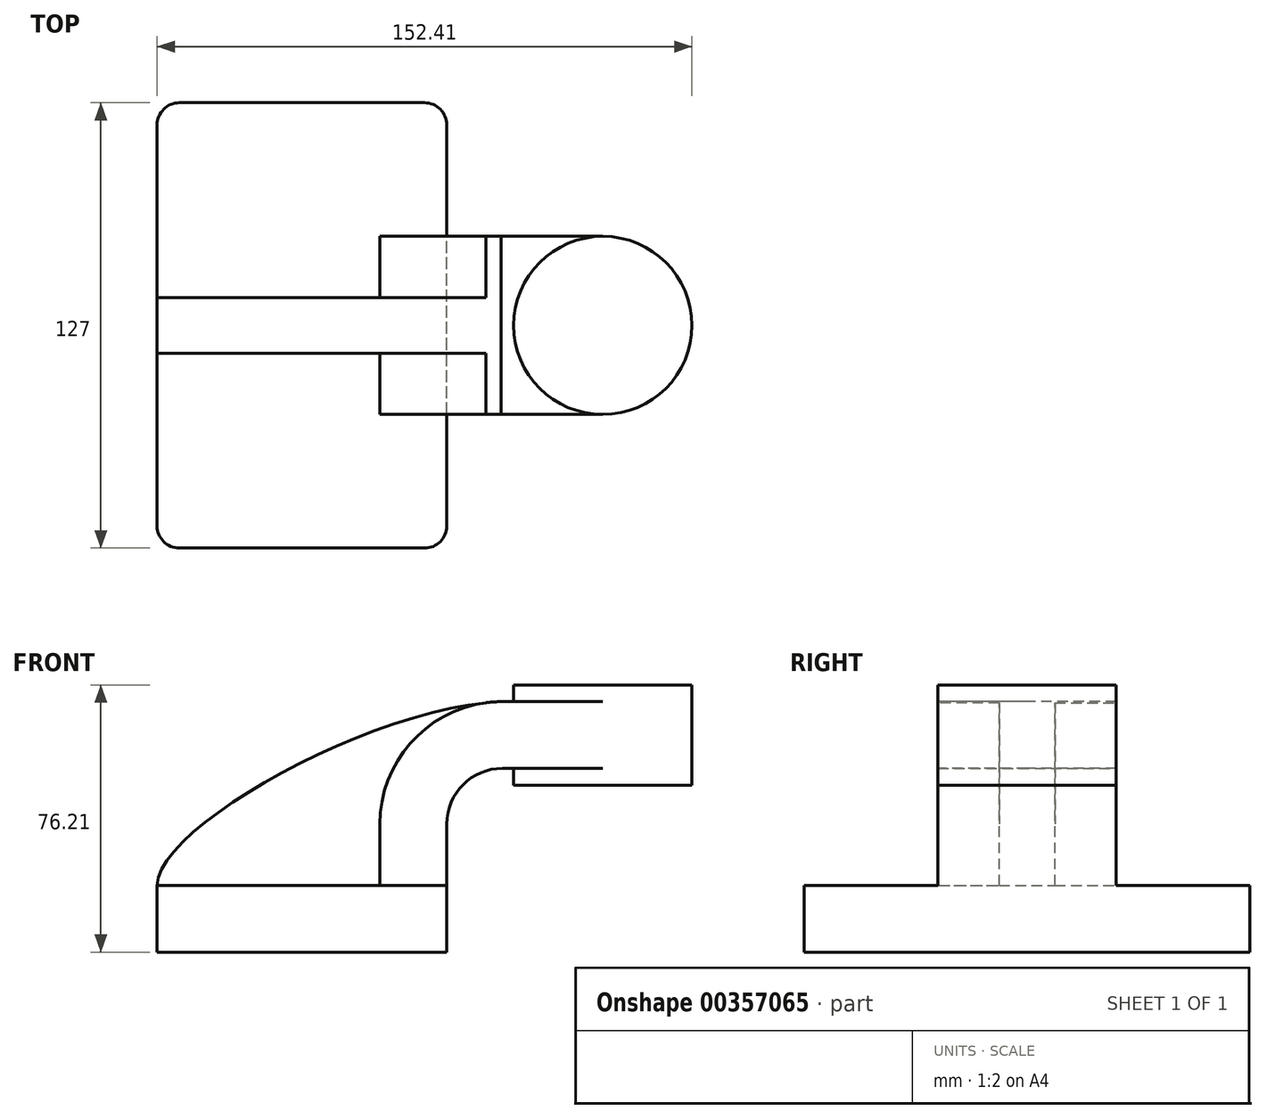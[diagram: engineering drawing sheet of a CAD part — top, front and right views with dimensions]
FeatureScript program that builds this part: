
annotation { "Feature Type Name" : "Feature", "Feature Type Description" : "" }
export const myFeature = defineFeature(function(context is Context, id is Id, definition is map)
    precondition{}
    {
        {
            var Q0;
            Q0=qCreatedBy(makeId("Front.planeOp"),FACE);
            var sketch = newSketch(context, id + "F0", { "sketchPlane" : qUnion([Q0])});
            skLineSegment(sketch, "E0.bottom", {"start": v(-41.28, 9.52) * mm, "end": v(41.27, 9.53) * mm});
            skLineSegment(sketch, "E0.top", {"start": v(-41.28, -9.53) * mm, "end": v(41.28, -9.53) * mm});
            skLineSegment(sketch, "E0.left", {"start": v(-41.28, 9.52) * mm, "end": v(-41.27, -9.53) * mm});
            skLineSegment(sketch, "E0.right", {"start": v(41.28, 9.53) * mm, "end": v(41.28, -9.52) * mm});
            skPoint(sketch, "E0.middle", {"position": v(0, 0) * mm});
            skLineSegment(sketch, "E1.bottom", {"start": v(111.12, 66.68) * mm, "end": v(60.32, 66.68) * mm});
            skLineSegment(sketch, "E1.top", {"start": v(111.12, 38.1) * mm, "end": v(60.33, 38.1) * mm});
            skLineSegment(sketch, "E1.left", {"start": v(111.12, 66.68) * mm, "end": v(111.12, 38.1) * mm});
            skLineSegment(sketch, "E1.right", {"start": v(60.32, 66.68) * mm, "end": v(60.33, 38.1) * mm});
            skPoint(sketch, "E1.middle", {"position": v(85.72, 52.39) * mm});
            skLineSegment(sketch, "E2", {"start": v(41.27, 9.53) * mm, "end": v(41.27, 27) * mm});
            skArc(sketch, "E3", {"start": v(41.27, 27) * mm, "mid": v(45.92, 38.23) * mm, "end": v(57.15, 42.88) * mm});
            skLineSegment(sketch, "E4", {"start": v(57.15, 42.88) * mm, "end": v(85.72, 42.88) * mm});
            skArc(sketch, "E5.0", {"start": v(22.22, 27) * mm, "mid": v(32.32, 51.56) * mm, "end": v(56.77, 61.92) * mm});
            skLineSegment(sketch, "E5.1", {"start": v(22.22, 9.53) * mm, "end": v(22.22, 27) * mm});
            skLineSegment(sketch, "E6", {"start": v(56.77, 61.92) * mm, "end": v(85.72, 61.92) * mm});
            skLineSegment(sketch, "E7", {"start": v(85.72, 38.1) * mm, "end": v(85.72, 66.68) * mm});
            skLineSegment(sketch, "E8", {"start": v(85.72, 66.68) * mm, "end": v(85.72, 61.92) * mm});
            skFitSpline(sketch, "E9", {"points": [v(-41.28, 9.52) * mm, v(56.77, 61.92) * mm], "startDerivative": vector(0.83, 50.51) * mm, "endDerivative": vector(110.6, 4.67) * mm});
            skSolve(sketch);
        }
        {
            var Q0;
            Q0=makeQuery(id+"F0.imprint","IMPRINT",FACE,{"disambiguationData":[TD([[makeQuery(id+"F0.imprint","IMPRINT",EDGE,{"derivedFrom":sQuery(id+"F0.wireOp",EDGE,"E0.top")}),1.0]])]});
            extrude(context, id + "F1", {"entities" : qUnion([Q0]), "endBound" : BoundingType.SYMMETRIC, "depth" : 127 * mm});
        }
        {
            var Q0;
            {var subQ1=sQuery(id+"F0.wireOp",EDGE,"E2");Q0=makeQuery(id+"F0.imprint","IMPRINT",FACE,{"disambiguationData":[TD([[makeQuery(id+"F0.imprint","IMPRINT",EDGE,{"derivedFrom":subQ1}),1.0]])]});}
            var Q1;
            {var subQ1=sQuery(id+"F0.wireOp",EDGE,"E6");var subQ3=sQuery(id+"F0.wireOp",EDGE,"E1.right");var subQ4=makeQuery(id+"F0.imprint","INTERSECT",VERTEX,{"derivedFrom":[subQ3,subQ1]});Q1=makeQuery(id+"F0.imprint","IMPRINT",FACE,{"disambiguationData":[TD([[makeQuery(id+"F0.imprint","IMPRINT",EDGE,{"disambiguationData":[TD([[subQ4,-1.0]])],"derivedFrom":subQ3}),1.0]])]});}
            extrude(context, id + "F2", {"entities" : qUnion([Q0, Q1]), "operationType" : NewBodyOperationType.ADD, "endBound" : BoundingType.SYMMETRIC, "depth" : 50.8 * mm});
        }
        {
            var Q0;
            {var subQ3=sQuery(id+"F0.wireOp",EDGE,"E5.1");Q0=makeQuery(id+"F0.imprint","IMPRINT",FACE,{"disambiguationData":[TD([[makeQuery(id+"F0.imprint","IMPRINT",EDGE,{"derivedFrom":subQ3}),1.0]])]});}
            extrude(context, id + "F3", {"entities" : qUnion([Q0]), "operationType" : NewBodyOperationType.ADD, "endBound" : BoundingType.SYMMETRIC, "depth" : 15.88 * mm});
        }
        {
            var Q0;
            {var subQ0=sQuery(id+"F0.wireOp",EDGE,"E1.left");Q0=makeQuery(id+"F0.imprint","IMPRINT",FACE,{"disambiguationData":[TD([[makeQuery(id+"F0.imprint","IMPRINT",EDGE,{"derivedFrom":subQ0}),-1.0]])]});}
            var Q1;
            Q1=sQuery(id+"F0.wireOp",EDGE,"E7");
            revolve(context, id + "F4", {"operationType" : NewBodyOperationType.ADD, "entities" : qUnion([Q0]), "axis" : qUnion([Q1]), "revolveType" : RevolveType.FULL});
        }
        {
            var Q0;
            Q0=makeQuery(id+"F1.opExtrude","CAP_EDGE",EDGE,{"disambiguationData":[OSD([sQuery(id+"F0.wireOp",EDGE,"E0.left")])],"isStart":false});
            var Q1;
            Q1=makeQuery(id+"F1.opExtrude","CAP_EDGE",EDGE,{"disambiguationData":[OSD([sQuery(id+"F0.wireOp",EDGE,"E0.right")])],"isStart":false});
            var Q2;
            Q2=makeQuery(id+"F1.opExtrude","CAP_EDGE",EDGE,{"disambiguationData":[OSD([sQuery(id+"F0.wireOp",EDGE,"E0.right")])],"isStart":true});
            var Q3;
            Q3=makeQuery(id+"F1.opExtrude","CAP_EDGE",EDGE,{"disambiguationData":[OSD([sQuery(id+"F0.wireOp",EDGE,"E0.left")])],"isStart":true});
            fillet(context, id + "F5", {"entities" : qUnion([Q0, Q1, Q2, Q3]), "radius" : 6.35 * mm, "tangentPropagation" : true, "allowEdgeOverflow" : false});
        }
    });
